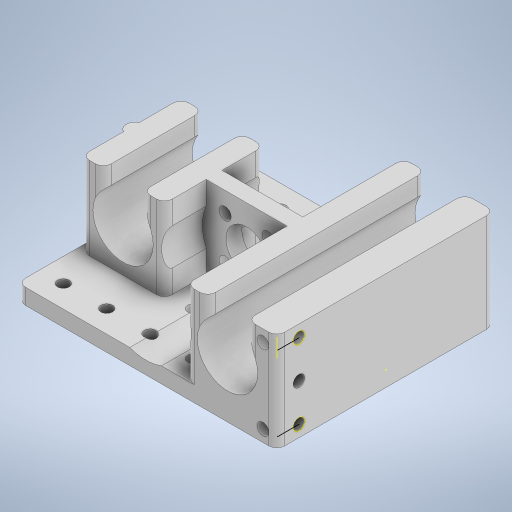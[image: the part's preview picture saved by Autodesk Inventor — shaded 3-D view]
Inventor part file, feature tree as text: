
AUTODESK INVENTOR PART (.ipt)
format: ipt  version: 2023 (Build 270158000, 158)  size: 514,048 bytes
history: native  units: mm
features: sketch x15, extrude x14, pattern_linear x2, pattern_circular x1, fillet x1
ambient origin geometry x8: Origin, YZ Plane, XZ Plane, XY Plane, X Axis, Y Axis, Z Axis, Center Point
bodies: Solid1 (feature_tree)
feature tree (33):
  extrude  "Extrusion1"  Depth=21.0mm
  extrude  "Extrusion4"  Depth=10.5mm
  extrude  "Extrusion5"  Depth=10.6mm TaperAngle=0.0deg
  pattern_circular  "Circular Pattern1"  Count=4 Angle=360.0deg
  extrude  "Extrusion6"  Depth=21.0mm
  extrude  "Extrusion7"  Depth=21.0mm TaperAngle=0.0deg
  extrude  "Extrusion8"  Depth=21.0mm
  extrude  "Extrusion9"  Depth=21.0mm TaperAngle=0.0deg
  extrude  "Extrusion10"  Depth=15.5mm
  extrude  "Extrusion14"  Depth=15.3mm
  pattern_linear  "Rectangular Pattern5"  Count1=10 Spacing1=0.0mm
  extrude  "Extrusion15"  Depth=55.2mm
  extrude  "Extrusion16"  Depth=10.0mm
  pattern_linear  "Rectangular Pattern6"  Spacing1=55.2mm  [1 undecoded]
  extrude  "Extrusion17"  Depth=10.0mm
  extrude  "Extrusion18"  Depth=2.0mm
  sketch  "Sketch32"  dims[d48=65.0mm d49=55.2mm]
  extrude  "Extrusion19"  Depth=2.0mm TaperAngle=0.0deg
  fillet  "Fillet1"  Radius=4.0mm
  sketch  "Sketch1"  dims[d0=65.0mm d1=21.0mm]
  sketch  "Sketch5"  dims[d2=4.0mm d3=0.0mm d16=10.5mm]
  sketch  "Sketch6"  dims[d17=10.5mm d18=10.6mm d19=0.0mm]
  sketch  "Sketch7"  dims[d20=7.7mm]
  sketch  "Sketch8"  dims[d21=45.0deg]
  sketch  "Sketch11"  dims[d22=3.1mm]
  sketch  "Sketch12"  dims[d23=10.6mm d24=0.0mm d25=40.0mm d26=360.0deg]
  sketch  "Sketch14"  dims[d28=15.5mm d29=21.0mm]
  sketch  "Sketch18"  dims[d30=21.0mm d31=25.6mm d32=29.6mm d33=0.0mm d34=0.0mm]
  sketch  "Sketch19"  dims[d35=15.5mm d36=21.0mm]
  sketch  "Sketch20"  dims[d37=21.0mm d38=10.6mm d39=14.6mm d40=0.0mm d41=0.0mm]
  sketch  "Sketch23"  dims[d42=15.5mm d43=15.5mm]
  sketch  "Sketch24"  dims[d44=15.3mm d45=15.3mm d46=100.0mm d47=0.0mm]
  sketch  "Sketch33"  dims[d50=4.0mm d51=0.0mm d52=10.0mm d53=55.2mm d54=10.0mm d55=25.2mm d56=5.0mm d57=0.0mm d98=4.0mm d99=3.0mm d100=4.0mm d101=0.0mm d102=60.0mm d104=11.0mm d105=50.0mm d107=11.0mm d108=2.0mm d109=0.0mm d110=3.0mm d111=90.0deg d112=2.9mm d113=3.0mm d114=0.0mm d115=30.0mm d117=9.5mm d118=22.5mm d119=30.0mm d120=0.0mm d121=22.5mm d122=30.0mm d123=0.0mm d124=3.5mm d125=3.0mm d126=3.0mm d127=3.5mm d128=3.0mm d129=0.0mm d130=2.0mm d12=0.5mm d13=0.872665mm d14=0.5mm d15=0.872665mm]
note: 1 required parameter value undecoded (feature->parameter linkage not recoverable at this tier; creation-order binding heuristic only, values carry confidence <= 0.55)
